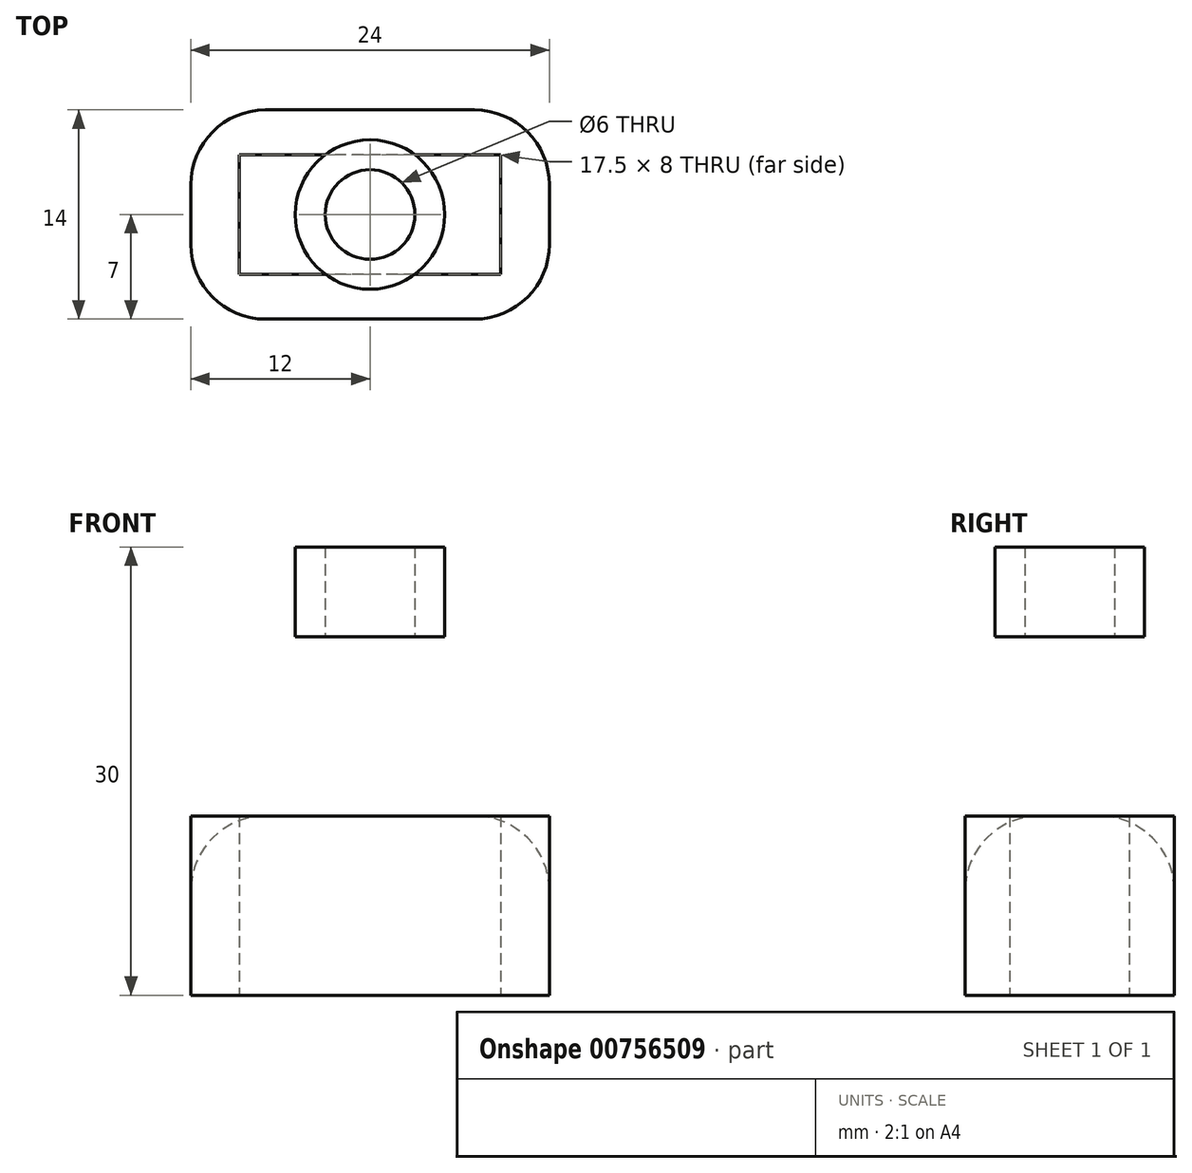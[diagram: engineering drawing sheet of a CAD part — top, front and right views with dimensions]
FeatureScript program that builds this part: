
annotation { "Feature Type Name" : "Feature", "Feature Type Description" : "" }
export const myFeature = defineFeature(function(context is Context, id is Id, definition is map)
    precondition{}
    {
        {
            var Q0;
            Q0=qCreatedBy(makeId("Top.planeOp"),FACE);
            var sketch = newSketch(context, id + "F0", { "sketchPlane" : qUnion([Q0])});
            skLineSegment(sketch, "E0.bottom", {"start": v(8.75, -4) * mm, "end": v(-8.75, -4) * mm});
            skLineSegment(sketch, "E0.top", {"start": v(8.75, 4) * mm, "end": v(-8.75, 4) * mm});
            skLineSegment(sketch, "E0.left", {"start": v(8.75, -4) * mm, "end": v(8.75, 4) * mm});
            skLineSegment(sketch, "E0.right", {"start": v(-8.75, -4) * mm, "end": v(-8.75, 4) * mm});
            skPoint(sketch, "E0.middle", {"position": v(0, 0) * mm});
            skLineSegment(sketch, "E1.bottom", {"start": v(12, -7) * mm, "end": v(-12, -7) * mm});
            skLineSegment(sketch, "E1.top", {"start": v(12, 7) * mm, "end": v(-12, 7) * mm});
            skLineSegment(sketch, "E1.left", {"start": v(12, -7) * mm, "end": v(12, 7) * mm});
            skLineSegment(sketch, "E1.right", {"start": v(-12, -7) * mm, "end": v(-12, 7) * mm});
            skSolve(sketch);
        }
        {
            var Q0;
            Q0 = qSketchRegion(id + "F0", true);
            extrude(context, id + "F1", {"entities" : qUnion([Q0]), "depth" : 12 * mm, "offsetDistance" : 25 * mm});
        }
        {
            var Q0;
            Q0=qCreatedBy(makeId("Top.planeOp"),FACE);
            var sketch = newSketch(context, id + "F2", { "sketchPlane" : qUnion([Q0])});
            skLineSegment(sketch, "E2.bottom", {"start": v(12, -7) * mm, "end": v(-12, -7) * mm});
            skLineSegment(sketch, "E2.top", {"start": v(12, 7) * mm, "end": v(-12, 7) * mm});
            skLineSegment(sketch, "E2.left", {"start": v(12, -7) * mm, "end": v(12, 7) * mm});
            skLineSegment(sketch, "E2.right", {"start": v(-12, -7) * mm, "end": v(-12, 7) * mm});
            skPoint(sketch, "E2.middle", {"position": v(0, 0) * mm});
            skSolve(sketch);
        }
        {
            var Q0;
            Q0 = qSketchRegion(id + "F2", true);
            extrude(context, id + "F3", {"entities" : qUnion([Q0]), "depth" : 12 * mm, "offsetDistance" : 25 * mm});
        }
        {
            var Q0;
            Q0=qCreatedBy(makeId("Top.planeOp"),FACE);
            var sketch = newSketch(context, id + "F4", { "sketchPlane" : qUnion([Q0])});
            skCircle(sketch, "E3", {"center": v(0, 0) * mm, "radius": 5 * mm});
            skSolve(sketch);
        }
        {
            var Q0;
            Q0 = qSketchRegion(id + "F4", true);
            extrude(context, id + "F5", {"entities" : qUnion([Q0]), "depth" : 6 * mm, "offsetDistance" : 25 * mm});
        }
        {
            var Q0;
            Q0=makeQuery(id+"F5.opExtrude","SWEPT_BODY",BODY,{"disambiguationData":[OSD([sQuery(id+"F4.wireOp",EDGE,"E3")])]});
            transform(context, id + "F6", {"entities" : qUnion([Q0]), "transformType" : TransformType.TRANSLATION_3D, "dx" : 0 * mm, "dy" : 0 * mm, "dz" : 12 * mm, "makeCopy" : false});
        }
        {
            var Q0;
            Q0=qCreatedBy(makeId("Top.planeOp"),FACE);
            var sketch = newSketch(context, id + "F7", { "sketchPlane" : qUnion([Q0])});
            skCircle(sketch, "E4", {"center": v(0, 0) * mm, "radius": 3 * mm});
            skSolve(sketch);
        }
        {
            var Q0;
            Q0 = qSketchRegion(id + "F7", true);
            extrude(context, id + "F8", {"entities" : qUnion([Q0]), "depth" : 25 * mm, "offsetDistance" : 25 * mm});
        }
        {
            var Q0;
            Q0=makeQuery(id+"F8.opExtrude","SWEPT_BODY",BODY,{"disambiguationData":[OSD([sQuery(id+"F7.wireOp",EDGE,"E4")])]});
            var Q1;
            Q1=makeQuery(id+"F5.opExtrude","SWEPT_BODY",BODY,{"disambiguationData":[OSD([sQuery(id+"F4.wireOp",EDGE,"E3")])]});
            booleanBodies(context, id + "F9", {"operationType" : BooleanOperationType.SUBTRACTION, "tools" : qUnion([Q0]), "targets" : qUnion([Q1])});
        }
        {
            var Q0;
            Q0=makeQuery(id+"F5.opExtrude","SWEPT_BODY",BODY,{"disambiguationData":[OSD([sQuery(id+"F4.wireOp",EDGE,"E3")])]});
            transform(context, id + "F10", {"entities" : qUnion([Q0]), "transformType" : TransformType.TRANSLATION_3D, "dx" : 0 * mm, "dy" : 0 * mm, "dz" : 12 * mm, "makeCopy" : false});
        }
        {
            var Q0;
            Q0=makeQuery(id+"F5.opExtrude","SWEPT_BODY",BODY,{"disambiguationData":[OSD([sQuery(id+"F4.wireOp",EDGE,"E3")])]});
            var Q1;
            Q1=makeQuery(id+"F1.opExtrude","SWEPT_BODY",BODY,{"disambiguationData":[OSD([sQuery(id+"F0.wireOp",EDGE,"E0.bottom"),sQuery(id+"F0.wireOp",EDGE,"E0.top"),sQuery(id+"F0.wireOp",EDGE,"E0.left"),sQuery(id+"F0.wireOp",EDGE,"E0.right"),sQuery(id+"F0.wireOp",EDGE,"E1.bottom"),sQuery(id+"F0.wireOp",EDGE,"E1.top"),sQuery(id+"F0.wireOp",EDGE,"E1.left"),sQuery(id+"F0.wireOp",EDGE,"E1.right")])]});
            booleanBodies(context, id + "F11", {"operationType" : BooleanOperationType.UNION, "tools" : qUnion([Q0, Q1])});
        }
        {
            var Q0;
            Q0=makeQuery(id+"F11.opBoolean","MERGE",EDGE,{"derivedFrom":[makeQuery(id+"F1.opExtrude","SWEPT_EDGE",EDGE,{"disambiguationData":[OSD([sQuery(id+"F0.wireOp",EDGE,"E1.bottom"),sQuery(id+"F0.wireOp",EDGE,"E1.right")])]}),makeQuery(id+"F3.opExtrude","SWEPT_EDGE",EDGE,{"disambiguationData":[OSD([sQuery(id+"F2.wireOp",EDGE,"E2.bottom"),sQuery(id+"F2.wireOp",EDGE,"E2.right")])]})]});
            var Q1;
            Q1=makeQuery(id+"F11.opBoolean","MERGE",EDGE,{"derivedFrom":[makeQuery(id+"F1.opExtrude","SWEPT_EDGE",EDGE,{"disambiguationData":[OSD([sQuery(id+"F0.wireOp",EDGE,"E1.bottom"),sQuery(id+"F0.wireOp",EDGE,"E1.left")])]}),makeQuery(id+"F3.opExtrude","SWEPT_EDGE",EDGE,{"disambiguationData":[OSD([sQuery(id+"F2.wireOp",EDGE,"E2.bottom"),sQuery(id+"F2.wireOp",EDGE,"E2.left")])]})]});
            var Q2;
            Q2=makeQuery(id+"F11.opBoolean","MERGE",EDGE,{"derivedFrom":[makeQuery(id+"F1.opExtrude","SWEPT_EDGE",EDGE,{"disambiguationData":[OSD([sQuery(id+"F0.wireOp",EDGE,"E1.top"),sQuery(id+"F0.wireOp",EDGE,"E1.right")])]}),makeQuery(id+"F3.opExtrude","SWEPT_EDGE",EDGE,{"disambiguationData":[OSD([sQuery(id+"F2.wireOp",EDGE,"E2.top"),sQuery(id+"F2.wireOp",EDGE,"E2.right")])]})]});
            var Q3;
            Q3=makeQuery(id+"F11.opBoolean","MERGE",EDGE,{"derivedFrom":[makeQuery(id+"F1.opExtrude","SWEPT_EDGE",EDGE,{"disambiguationData":[OSD([sQuery(id+"F0.wireOp",EDGE,"E1.top"),sQuery(id+"F0.wireOp",EDGE,"E1.left")])]}),makeQuery(id+"F3.opExtrude","SWEPT_EDGE",EDGE,{"disambiguationData":[OSD([sQuery(id+"F2.wireOp",EDGE,"E2.top"),sQuery(id+"F2.wireOp",EDGE,"E2.left")])]})]});
            var Q4;
            Q4=makeQuery(id+"F3.opExtrude","CAP_EDGE",EDGE,{"disambiguationData":[OSD([sQuery(id+"F2.wireOp",EDGE,"E2.bottom")])],"isStart":false});
            var Q5;
            Q5=makeQuery(id+"F3.opExtrude","CAP_EDGE",EDGE,{"disambiguationData":[OSD([sQuery(id+"F2.wireOp",EDGE,"E2.right")])],"isStart":false});
            var Q6;
            Q6=makeQuery(id+"F3.opExtrude","CAP_EDGE",EDGE,{"disambiguationData":[OSD([sQuery(id+"F2.wireOp",EDGE,"E2.top")])],"isStart":false});
            var Q7;
            Q7=makeQuery(id+"F3.opExtrude","CAP_EDGE",EDGE,{"disambiguationData":[OSD([sQuery(id+"F2.wireOp",EDGE,"E2.left")])],"isStart":false});
            fillet(context, id + "F12", {"entities" : qUnion([Q0, Q1, Q2, Q3, Q4, Q5, Q6, Q7]), "radius" : 5 * mm, "tangentPropagation" : true, "allowEdgeOverflow" : false});
        }
    });
